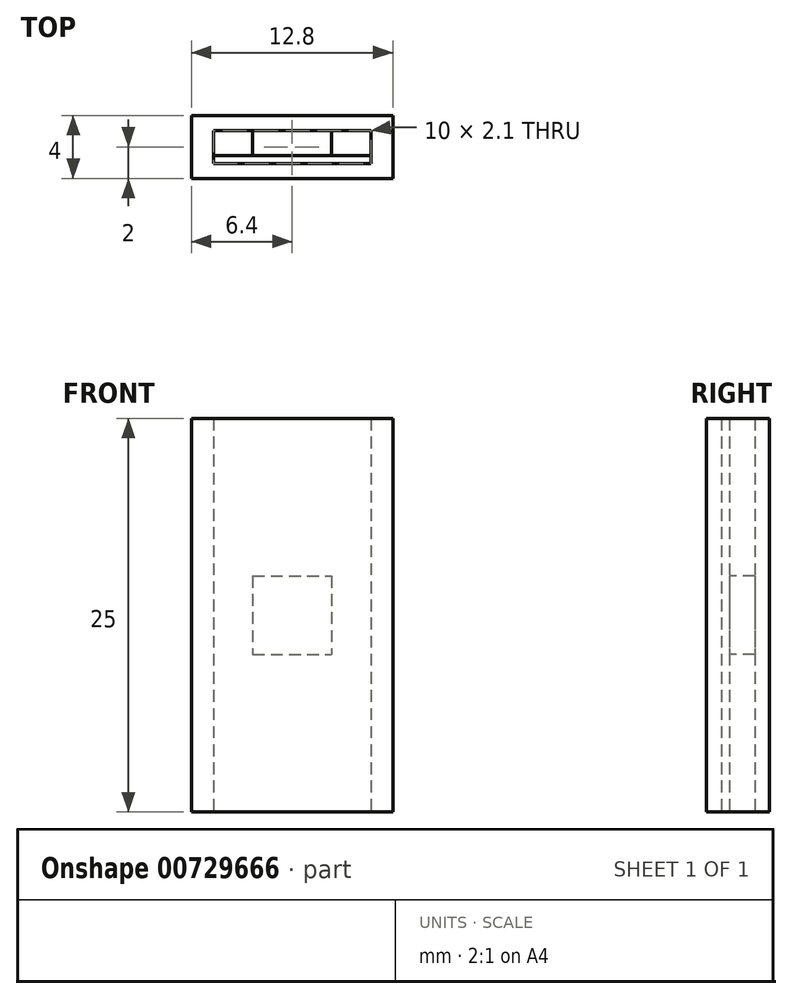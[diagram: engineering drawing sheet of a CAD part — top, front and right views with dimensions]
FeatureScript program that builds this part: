
annotation { "Feature Type Name" : "Feature", "Feature Type Description" : "" }
export const myFeature = defineFeature(function(context is Context, id is Id, definition is map)
    precondition{}
    {
        {
            var Q0;
            Q0=qCreatedBy(makeId("Top.planeOp"),FACE);
            var sketch = newSketch(context, id + "F0", { "sketchPlane" : qUnion([Q0])});
            skLineSegment(sketch, "E0.bottom", {"start": v(-5, 0.5) * mm, "end": v(5, 0.5) * mm});
            skLineSegment(sketch, "E0.top", {"start": v(-5, 0) * mm, "end": v(5, 0) * mm});
            skLineSegment(sketch, "E0.left", {"start": v(-5, 0.5) * mm, "end": v(-5, 0) * mm});
            skLineSegment(sketch, "E0.right", {"start": v(5, 0.5) * mm, "end": v(5, 0) * mm});
            skLineSegment(sketch, "E1.bottom", {"start": v(-2.5, 2.1) * mm, "end": v(2.5, 2.1) * mm});
            skLineSegment(sketch, "E1.top", {"start": v(-2.5, 0.5) * mm, "end": v(2.5, 0.5) * mm});
            skLineSegment(sketch, "E1.left", {"start": v(-2.5, 2.1) * mm, "end": v(-2.5, 0.5) * mm});
            skLineSegment(sketch, "E1.right", {"start": v(2.5, 2.1) * mm, "end": v(2.5, 0.5) * mm});
            skSolve(sketch);
        }
        {
            var Q0;
            Q0=makeQuery(id+"F0.imprint","IMPRINT",FACE,{"disambiguationData":[TD([[makeQuery(id+"F0.imprint","IMPRINT",EDGE,{"derivedFrom":sQuery(id+"F0.wireOp",EDGE,"E0.top")}),1.0]])]});
            extrude(context, id + "F1", {"entities" : qUnion([Q0]), "endBound" : BoundingType.SYMMETRIC, "depth" : 25 * mm, "offsetDistance" : 25 * mm});
        }
        {
            var Q0;
            Q0=makeQuery(id+"F0.imprint","IMPRINT",FACE,{"disambiguationData":[TD([[makeQuery(id+"F0.imprint","IMPRINT",EDGE,{"derivedFrom":sQuery(id+"F0.wireOp",EDGE,"E1.bottom")}),-1.0]])]});
            extrude(context, id + "F2", {"entities" : qUnion([Q0]), "operationType" : NewBodyOperationType.ADD, "endBound" : BoundingType.SYMMETRIC, "depth" : 5 * mm, "offsetDistance" : 25 * mm});
        }
        {
            var Q0;
            Q0=qCreatedBy(makeId("Top.planeOp"),FACE);
            var sketch = newSketch(context, id + "F3", { "sketchPlane" : qUnion([Q0])});
            skLineSegment(sketch, "E2.bottom", {"start": v(-5, 2.1) * mm, "end": v(5, 2.1) * mm});
            skLineSegment(sketch, "E2.top", {"start": v(-5, 0) * mm, "end": v(5, 0) * mm});
            skLineSegment(sketch, "E2.left", {"start": v(-5, 2.1) * mm, "end": v(-5, 0) * mm});
            skLineSegment(sketch, "E2.right", {"start": v(5, 2.1) * mm, "end": v(5, 0) * mm});
            skLineSegment(sketch, "E3.bottom", {"start": v(6.4, -0.95) * mm, "end": v(-6.4, -0.95) * mm});
            skLineSegment(sketch, "E3.top", {"start": v(6.4, 3.05) * mm, "end": v(-6.4, 3.05) * mm});
            skLineSegment(sketch, "E3.left", {"start": v(6.4, -0.95) * mm, "end": v(6.4, 3.05) * mm});
            skLineSegment(sketch, "E3.right", {"start": v(-6.4, -0.95) * mm, "end": v(-6.4, 3.05) * mm});
            skLineSegment(sketch, "E4", {"start": v(-5, 1.05) * mm, "end": v(5, 1.05) * mm});
            skSolve(sketch);
        }
        {
            var Q0;
            Q0=makeQuery(id+"F3.imprint","IMPRINT",FACE,{"disambiguationData":[TD([[makeQuery(id+"F3.imprint","IMPRINT",EDGE,{"derivedFrom":sQuery(id+"F3.wireOp",EDGE,"E2.bottom")}),1.0]])]});
            extrude(context, id + "F4", {"entities" : qUnion([Q0]), "endBound" : BoundingType.SYMMETRIC, "depth" : 25 * mm, "offsetDistance" : 25 * mm});
        }
    });
